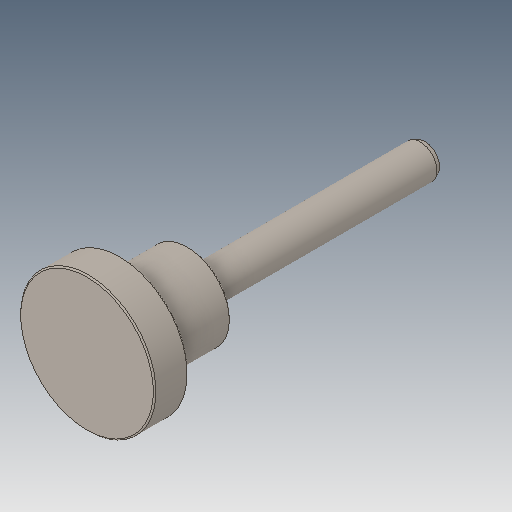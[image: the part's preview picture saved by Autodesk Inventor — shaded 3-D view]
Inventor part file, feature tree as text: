
AUTODESK INVENTOR PART (.ipt)
format: ipt  version: 2023.5 (Build 275446000, 446)  size: 115,712 bytes
history: native  units: in
note: dims shown in document units (in); Inventor stores cm internally (conversion verified against a paired STEP export)
features: fillet x1
ambient origin geometry x8: Origin, YZ Plane, XZ Plane, XY Plane, X Axis, Y Axis, Z Axis, Center Point
bodies: Solid1 (feature_tree)
feature tree (1):
  fillet  "Fillet1"  [1 undecoded]
note: 1 required parameter value undecoded (feature->parameter linkage not recoverable at this tier; creation-order binding heuristic only, values carry confidence <= 0.55)
